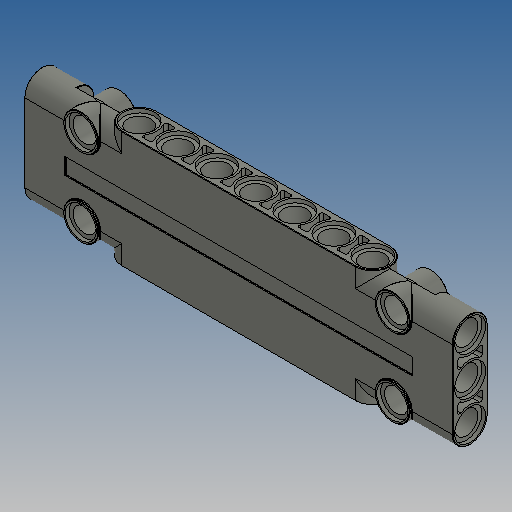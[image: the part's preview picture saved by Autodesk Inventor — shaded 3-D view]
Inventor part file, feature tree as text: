
AUTODESK INVENTOR PART (.ipt)
format: ipt  version: 2025 (Build 290162010, 162A)  size: 1,081,344 bytes
history: native  units: in
note: dims shown in document units (in); Inventor stores cm internally (conversion verified against a paired STEP export)
features: extrude x16, sketch x11, mirror x3, plane x1, fillet x1
ambient origin geometry x8: Origin, YZ Plane, XZ Plane, XY Plane, X Axis, Y Axis, Z Axis, Center Point
bodies: Solid1 (feature_tree)
feature tree (32):
  extrude  "Extrusion1"  Depth=0.189in
  sketch  "Sketch3"  dims[d6=0.189in d7=0.252in]
  extrude  "Extrusion2"  Depth=0.0315in
  extrude  "Extrusion3"  TaperAngle=0.0deg  [1 undecoded]
  extrude  "Extrusion4"  Depth=0.252in
  plane  "Work Plane1"
  extrude  "Extrusion5"  Depth=0.7874in
  sketch  "Sketch5"  dims[d12=0.3937in d14=0.3937in d16=0.2835in]
  extrude  "Extrusion6"  Depth=0.2835in
  extrude  "Extrusion7"  Depth=0.0315in
  extrude  "Extrusion10"  Depth=0.2205in TaperAngle=0.0deg
  extrude  "Extrusion8"  Depth=0.189in
  extrude  "Extrusion9"  Depth=0.0315in TaperAngle=0.0deg
  mirror  "Mirror1"
  mirror  "Mirror2"
  sketch  "Sketch8"  dims[d22=-0.1417in d23=0.189in]
  extrude  "Extrusion11"  Depth=0.189in
  extrude  "Extrusion12"  Depth=0.0157in
  extrude  "Extrusion13"  Depth=0.2677in
  sketch  "Sketch9"  dims[d24=0.2835in d25=0.0315in d26=0.0in]
  extrude  "Extrusion14"  TaperAngle=0.0deg  [1 undecoded]
  extrude  "Extrusion16"  Depth=0.2677in TaperAngle=0.0deg
  mirror  "Mirror3"
  extrude  "Extrusion15"  Depth=0.252in
  fillet  "Fillet1"  Radius=0.0315in
  sketch  "Sketch2"  dims[d2=0.2835in d3=0.0315in]
  sketch  "Skizze - Rechteckige Anordnung1"  dims[d0=0.315in d1=0.189in]
  sketch  "Sketch4"  dims[d8=45.0deg d9=0.7874in d11=0.315in]
  sketch  "Sketch6"  dims[d17=0.0in d18=0.0315in]
  sketch  "Sketch7"  dims[d19=0.0in d20=0.2205in d21=0.0in]
  sketch  "Sketch10"  dims[d27=0.2835in d28=0.189in d29=1.2598in d30=0.2677in d31=0.0472in d32=0.0in d33=0.0in d34=0.2677in d35=0.0in d36=0.252in d37=0.0315in d38=0.0in d39=0.252in d40=0.0315in d41=0.0in d42=0.0315in d43=0.2205in d44=0.0in d45=0.2835in d46=1.8898in d47=0.189in d48=0.1417in d49=0.1417in d50=0.0in d51=0.0in d52=0.1417in d53=0.0in d54=0.315in d55=0.0in d56=0.252in d57=0.0315in d58=0.0in d59=2.8031in d60=0.126in d62=0.0079in d63=0.0in d64=45.0deg d65=2.3622in d67=0.315in d68=0.3937in d70=0.3937in d72=0.2205in d73=0.0in d74=0.0039in d75=0.0157in]
  sketch  "Skizze - Rechteckige Anordnung2"  dims[d4=3.4646in d5=0.0in]
note: 2 required parameter values undecoded (feature->parameter linkage not recoverable at this tier; creation-order binding heuristic only, values carry confidence <= 0.55)
